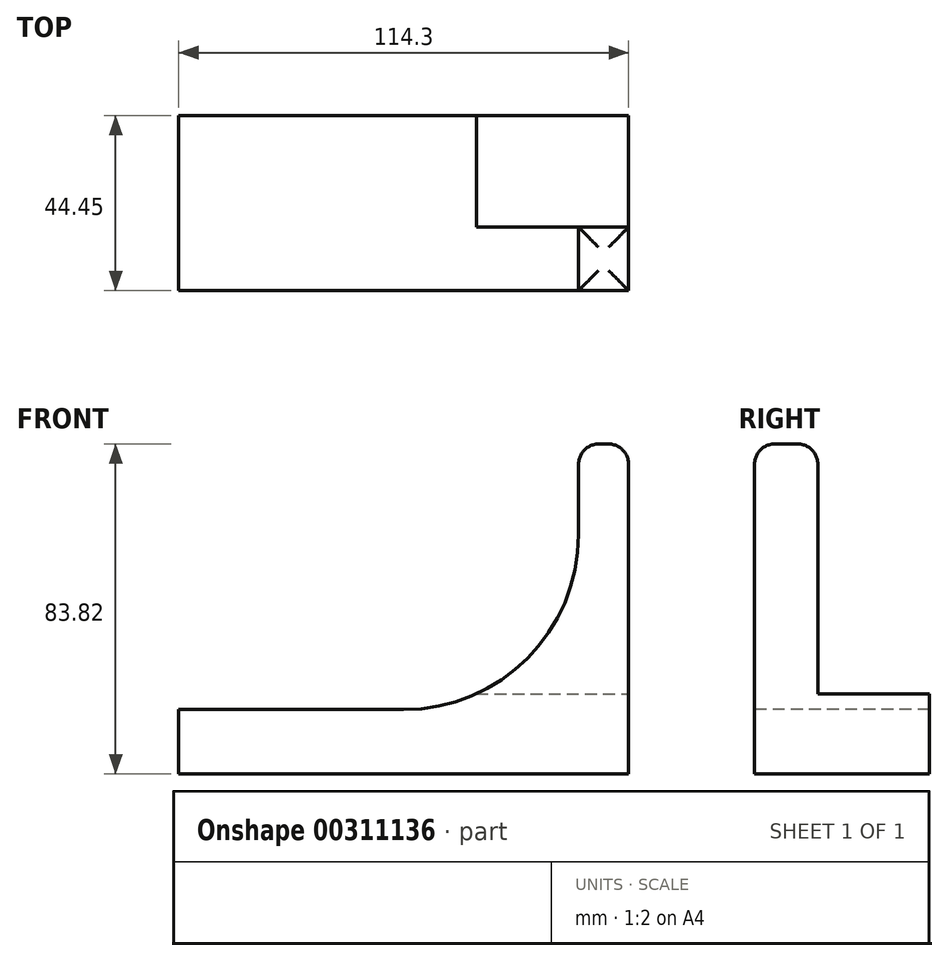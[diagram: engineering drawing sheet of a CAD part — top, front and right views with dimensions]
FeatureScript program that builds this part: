
annotation { "Feature Type Name" : "Feature", "Feature Type Description" : "" }
export const myFeature = defineFeature(function(context is Context, id is Id, definition is map)
    precondition{}
    {
        {
            var Q0;
            Q0=qCreatedBy(makeId("Front.planeOp"),FACE);
            var sketch = newSketch(context, id + "F0", { "sketchPlane" : qUnion([Q0])});
            skLineSegment(sketch, "E0.bottom", {"start": v(0, 0) * mm, "end": v(114.3, 0) * mm});
            skLineSegment(sketch, "E0.left", {"start": v(0, 0) * mm, "end": v(0, 83.82) * mm});
            skLineSegment(sketch, "E0.right", {"start": v(114.3, 0) * mm, "end": v(114.3, 83.82) * mm});
            skLineSegment(sketch, "E1", {"start": v(114.3, 83.82) * mm, "end": v(101.6, 83.82) * mm});
            skLineSegment(sketch, "E2", {"start": v(0, 83.82) * mm, "end": v(12.7, 83.82) * mm});
            skLineSegment(sketch, "E3", {"start": v(12.7, 83.82) * mm, "end": v(12.7, 60.8) * mm});
            skLineSegment(sketch, "E4", {"start": v(101.6, 83.82) * mm, "end": v(101.6, 60.8) * mm});
            skPoint(sketch, "E5.first.point", {"position": v(57.15, 16.34) * mm});
            skArc(sketch, "E6", {"start": v(12.7, 60.8) * mm, "mid": v(57.15, 16.34) * mm, "end": v(101.6, 60.8) * mm});
            skSolve(sketch);
        }
        {
            var Q0;
            Q0=makeQuery(id+"F0.imprint","IMPRINT",FACE,{"disambiguationData":[TD([[makeQuery(id+"F0.imprint","IMPRINT",EDGE,{"derivedFrom":sQuery(id+"F0.wireOp",EDGE,"E0.bottom")}),1.0]])]});
            extrude(context, id + "F1", {"entities" : qUnion([Q0]), "oppositeDirection" : true, "depth" : 44.45 * mm});
        }
        {
            var Q0;
            Q0=makeQuery(id+"F1.opExtrude","SWEPT_FACE",FACE,{"disambiguationData":[OSD([sQuery(id+"F0.wireOp",EDGE,"E0.right")])]});
            var sketch = newSketch(context, id + "F2", { "sketchPlane" : qUnion([Q0])});
            skLineSegment(sketch, "E7.bottom", {"start": v(16.07, 20.37) * mm, "end": v(44.45, 20.37) * mm});
            skLineSegment(sketch, "E7.top", {"start": v(16.07, 83.82) * mm, "end": v(44.45, 83.82) * mm});
            skLineSegment(sketch, "E7.left", {"start": v(16.07, 20.37) * mm, "end": v(16.07, 83.82) * mm});
            skLineSegment(sketch, "E7.right", {"start": v(44.45, 20.37) * mm, "end": v(44.45, 83.82) * mm});
            skSolve(sketch);
        }
        {
            var Q0;
            Q0=makeQuery(id+"F2.imprint","IMPRINT",FACE,{"disambiguationData":[TD([[makeQuery(id+"F2.imprint","IMPRINT",EDGE,{"derivedFrom":sQuery(id+"F2.wireOp",EDGE,"E7.bottom")}),1.0]])]});
            extrude(context, id + "F3", {"entities" : qUnion([Q0]), "operationType" : NewBodyOperationType.REMOVE, "oppositeDirection" : true, "depth" : 114.3 * mm});
        }
        {
            var Q0;
            Q0=makeQuery(id+"F1.opExtrude","CAP_FACE",FACE,{"disambiguationData":[OSD([sQuery(id+"F0.wireOp",EDGE,"E0.bottom"),sQuery(id+"F0.wireOp",EDGE,"E0.left"),sQuery(id+"F0.wireOp",EDGE,"E0.right"),sQuery(id+"F0.wireOp",EDGE,"E1"),sQuery(id+"F0.wireOp",EDGE,"E2"),sQuery(id+"F0.wireOp",EDGE,"E3"),sQuery(id+"F0.wireOp",EDGE,"E4"),sQuery(id+"F0.wireOp",EDGE,"E6")])],"isStart":true});
            var sketch = newSketch(context, id + "F4", { "sketchPlane" : qUnion([Q0])});
            skLineSegment(sketch, "E8", {"start": v(57.15, 16.34) * mm, "end": v(0, 16.34) * mm});
            skLineSegment(sketch, "E9", {"start": v(0, 16.34) * mm, "end": v(0, 83.82) * mm});
            skLineSegment(sketch, "E10", {"start": v(0, 83.82) * mm, "end": v(12.7, 83.82) * mm});
            skLineSegment(sketch, "E11", {"start": v(12.7, 83.82) * mm, "end": v(57.15, 16.34) * mm});
            skSolve(sketch);
        }
        {
            var Q0;
            {var subQ1=sQuery(id+"F4.wireOp",EDGE,"E8");Q0=makeQuery(id+"F4.imprint","IMPRINT",FACE,{"disambiguationData":[TD([[makeQuery(id+"F4.imprint","IMPRINT",EDGE,{"derivedFrom":subQ1}),-1.0]])]});}
            extrude(context, id + "F5", {"entities" : qUnion([Q0]), "operationType" : NewBodyOperationType.REMOVE, "oppositeDirection" : true, "depth" : 127 * mm});
        }
        {
            var Q0;
            Q0=makeQuery(id+"F1.opExtrude","SWEPT_FACE",FACE,{"disambiguationData":[OSD([sQuery(id+"F0.wireOp",EDGE,"E1")])]});
            fillet(context, id + "F6", {"entities" : qUnion([Q0]), "radius" : 5.08 * mm, "tangentPropagation" : true, "allowEdgeOverflow" : false});
        }
    });
